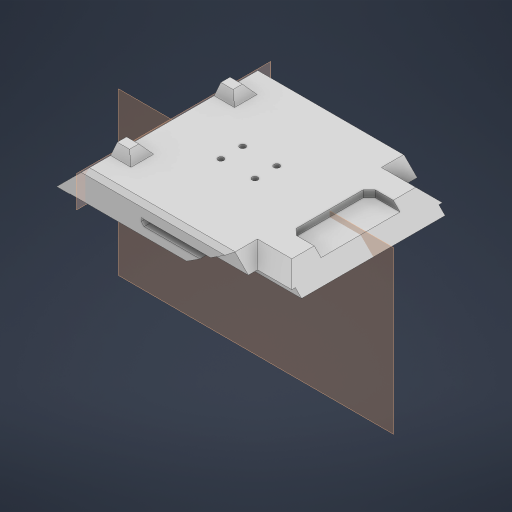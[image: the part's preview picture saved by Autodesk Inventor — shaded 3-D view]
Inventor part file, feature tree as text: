
AUTODESK INVENTOR PART (.ipt)
format: ipt  version: 2024 (Build 280153000, 153)  size: 437,760 bytes
history: native  units: in
note: dims shown in document units (in); Inventor stores cm internally (conversion verified against a paired STEP export)
features: reference x23, sketch x12, extrude x12, plane x7, projected_geometry x6, other x5, chamfer x2, mirror x1, fillet x1
ambient origin geometry x8: Origin, YZ Plane, XZ Plane, XY Plane, X Axis, Y Axis, Z Axis, Center Point
bodies: Solid1 (feature_tree)
feature tree (69):
  sketch  "Sketch1"  dims[d0=0.0118in d1=0.0118in]
  plane  "Work Plane1"
  extrude  "Extrusion1"  Depth=0.0118in
  plane  "Work Plane2"
  extrude  "Extrusion2"  Depth=0.0118in TaperAngle=0.0deg
  sketch  "Sketch3"  dims[d5=135.0deg d6=1.0in d7=0.0in]
  plane  "Work Plane3"
  extrude  "Extrusion3"  Depth=1.0in TaperAngle=0.0deg
  sketch  "Sketch4"  dims[d8=1.0in d9=0.0in d10=1.0in d11=0.0in]
  plane  "Work Plane4"
  extrude  "Extrusion4"  Depth=1.0in TaperAngle=0.0deg
  plane  "Work Plane5"
  extrude  "Extrusion5"  Depth=0.0118in
  chamfer  "Chamfer1"  Distance=6.4375in
  sketch  "Sketch8"  dims[d16=0.1181in d17=0.125in d18=45.0deg d19=6.4375in d20=0.0in]
  plane  "Work Plane6"
  extrude  "Extrusion6"  Depth=6.4375in TaperAngle=0.0deg
  mirror  "Mirror2"
  extrude  "Extrusion7"  Depth=0.0984in
  extrude  "Extrusion8"  Depth=0.2362in TaperAngle=0.0deg
  extrude  "Extrusion9"  Depth=0.2047in
  extrude  "Extrusion10"  Depth=2.1112in TaperAngle=0.0deg
  fillet  "Fillet1"  [1 undecoded]
  extrude  "Extrusion11"  Depth=0.0394in
  plane  "Work Plane7"
  extrude  "Extrusion12"  Depth=0.2362in
  chamfer  "Chamfer2"  Distance=0.1654in
  reference  "Reference1"
  reference  "Reference2"
  reference  "Reference3"
  reference  "Reference4"
  reference  "Reference5"
  reference  "Reference6"
  sketch  "Sketch2"  dims[d2=0.0118in d3=0.1875in d4=0.0in]
  reference  "Reference7"
  reference  "Reference8"
  reference  "Reference9"
  reference  "Reference10"
  reference  "Reference11"
  reference  "Reference12"
  reference  "Reference13"
  reference  "Reference14"
  reference  "Reference15"
  reference  "Reference16"
  reference  "Reference17"
  reference  "Reference18"
  reference  "Reference19"
  sketch  "Sketch6"  dims[d12=0.1969in d13=0.0118in d14=6.4375in d15=0.0in]
  reference  "Reference21"
  reference  "Reference22"
  reference  "Reference23"
  reference  "Reference25"
  sketch  "Sketch10"  dims[d23=0.1654in d24=0.0984in]
  sketch  "Sketch11"  dims[d25=0.0197in d26=0.2362in d27=0.0in]
  projected_geometry  "Projected Loop2"
  projected_geometry  "Projected Loop3"
  sketch  "Sketch13"  dims[d28=0.2047in d29=0.2047in]
  projected_geometry  "Projected Loop4"
  projected_geometry  "Projected Loop5"
  sketch  "Sketch14"  dims[d30=1.2362in d31=0.0in d32=2.1112in d33=0.0in d34=45.0deg]
  projected_geometry  "Projected Loop6"
  sketch  "Sketch15"  dims[d35=1.0in d36=0.0in d37=0.0394in]
  projected_geometry  "Projected Loop7"
  sketch  "Sketch16"  dims[d38=0.315in d39=0.315in d40=0.1654in d41=0.1654in d42=0.1654in d43=0.1654in d44=0.9843in d45=0.9843in d46=1.0in d47=0.0in d48=90.0deg d49=0.2362in d50=0.5906in d51=0.0in d52=0.2362in d53=0.125in d54=45.0deg]
  other  "<userpath>\Desktop\SeniorDesign\Head_V3\Head_V3_Assembly.iam"
  other  "Head_V3_Assembly.iam"
  other  "Head_Backplate:1"
  other  "Head_Left_Panel:1"
  other  "Head_base_mount:1"
note: 1 required parameter value undecoded (feature->parameter linkage not recoverable at this tier; creation-order binding heuristic only, values carry confidence <= 0.55)
